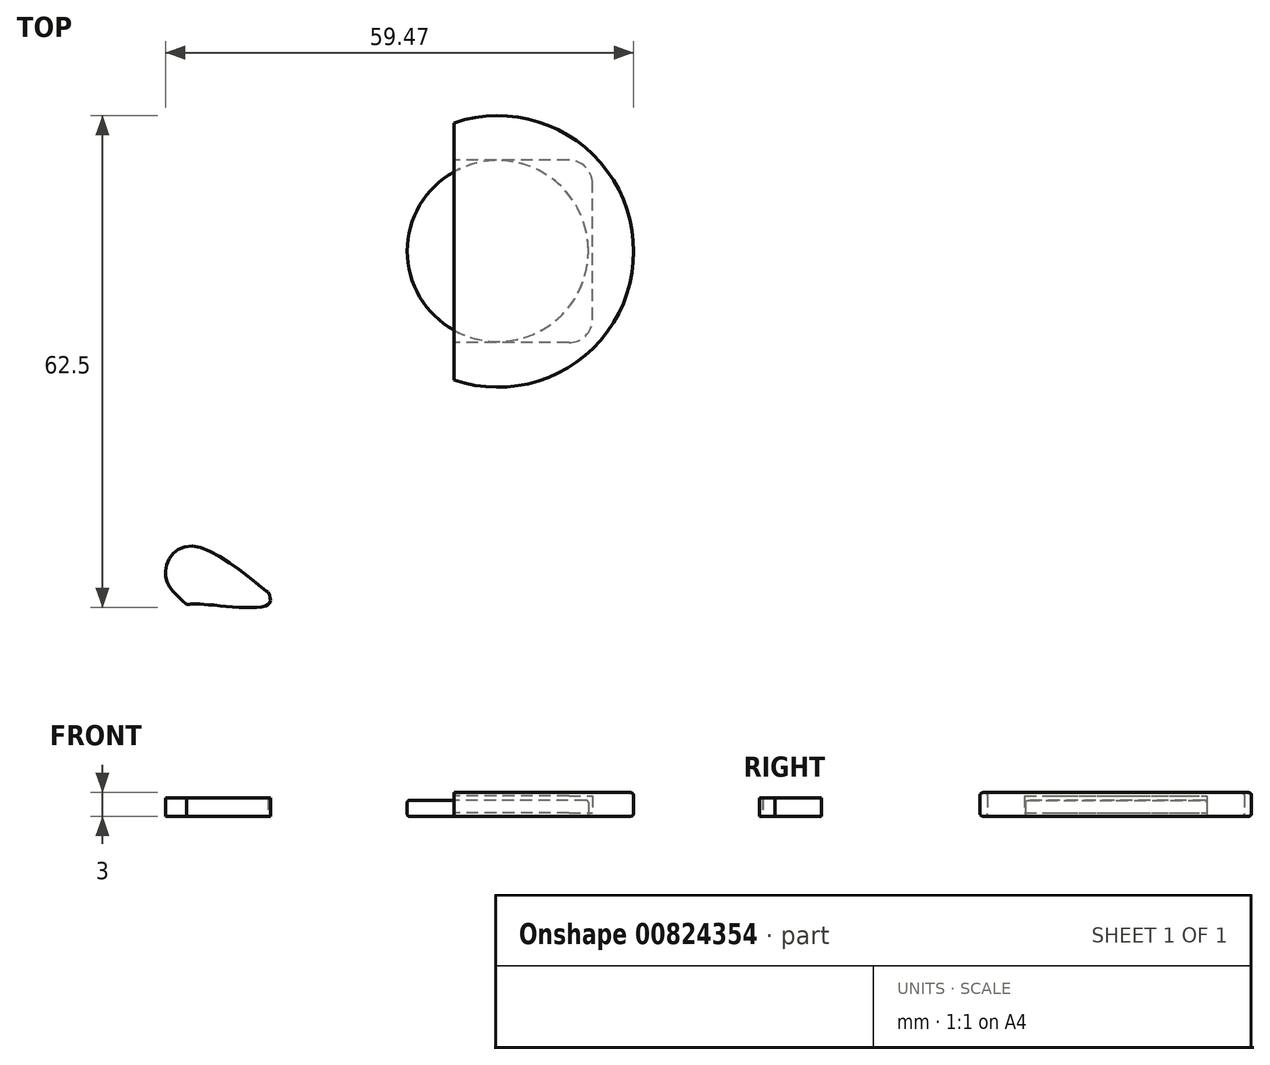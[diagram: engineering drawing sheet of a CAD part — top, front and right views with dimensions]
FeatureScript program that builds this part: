
annotation { "Feature Type Name" : "Feature", "Feature Type Description" : "" }
export const myFeature = defineFeature(function(context is Context, id is Id, definition is map)
    precondition{}
    {
        {
            var Q0;
            Q0=qCreatedBy(makeId("Top.planeOp"),FACE);
            var sketch = newSketch(context, id + "F0", { "sketchPlane" : qUnion([Q0])});
            skCircle(sketch, "E0", {"center": v(0, 0) * mm, "radius": 11.5 * mm});
            skSolve(sketch);
        }
        {
            var Q0;
            Q0=makeQuery(id+"F0.imprint","IMPRINT",FACE,{"disambiguationData":[TD([[makeQuery(id+"F0.imprint","IMPRINT",EDGE,{"derivedFrom":sQuery(id+"F0.wireOp",EDGE,"E0")}),1.0]])]});
            extrude(context, id + "F1", {"entities" : qUnion([Q0]), "depth" : 2 * mm, "offsetDistance" : 25 * mm});
        }
        {
            var Q0;
            Q0=makeQuery(id+"F1.opExtrude","CAP_EDGE",EDGE,{"disambiguationData":[OSD([sQuery(id+"F0.wireOp",EDGE,"E0")])],"isStart":false});
            var Q1;
            Q1=makeQuery(id+"F1.opExtrude","CAP_EDGE",EDGE,{"disambiguationData":[OSD([sQuery(id+"F0.wireOp",EDGE,"E0")])],"isStart":true});
            fillet(context, id + "F2", {"entities" : qUnion([Q0, Q1]), "radius" : 0.25 * mm, "tangentPropagation" : true, "allowEdgeOverflow" : false});
        }
        {
            var Q0;
            Q0=makeQuery(id+"F1.opExtrude","SWEPT_BODY",BODY,{"disambiguationData":[OSD([sQuery(id+"F0.wireOp",EDGE,"E0")])]});
            transform(context, id + "F3", {"entities" : qUnion([Q0]), "transformType" : TransformType.TRANSLATION_3D, "dx" : 0 * mm, "dy" : 36.3 * mm, "dz" : 0 * mm, "makeCopy" : true});
        }
        {
            var Q0;
            Q0=qCreatedBy(makeId("Top.planeOp"),FACE);
            var sketch = newSketch(context, id + "F4", { "sketchPlane" : qUnion([Q0])});
            skLineSegment(sketch, "E1.bottom", {"start": v(-15.7, 51.26) * mm, "end": v(-3.72, 51.26) * mm});
            skLineSegment(sketch, "E1.top", {"start": v(-15.7, 20.78) * mm, "end": v(-3.72, 20.78) * mm});
            skLineSegment(sketch, "E1.left", {"start": v(-15.7, 51.26) * mm, "end": v(-15.7, 20.78) * mm});
            skLineSegment(sketch, "E1.right", {"start": v(-3.72, 51.26) * mm, "end": v(-3.72, 20.78) * mm});
            skSolve(sketch);
        }
        {
            var Q0;
            Q0=makeQuery(id+"F4.imprint","IMPRINT",FACE,{"disambiguationData":[TD([[makeQuery(id+"F4.imprint","IMPRINT",EDGE,{"derivedFrom":sQuery(id+"F4.wireOp",EDGE,"E1.bottom")}),-1.0]])]});
            extrude(context, id + "F5", {"entities" : qUnion([Q0]), "depth" : 2 * mm, "offsetDistance" : 25 * mm});
        }
        {
            var Q0;
            Q0=makeQuery(id+"F5.opExtrude","SWEPT_BODY",BODY,{"disambiguationData":[OSD([sQuery(id+"F4.wireOp",EDGE,"E1.bottom"),sQuery(id+"F4.wireOp",EDGE,"E1.top"),sQuery(id+"F4.wireOp",EDGE,"E1.left"),sQuery(id+"F4.wireOp",EDGE,"E1.right")])]});
            var Q1;
            Q1=makeQuery(id+"F3.opPattern","COPY",BODY,{"derivedFrom":makeQuery(id+"F1.opExtrude","SWEPT_BODY",BODY,{"disambiguationData":[OSD([sQuery(id+"F0.wireOp",EDGE,"E0")])]}),"instanceName":"1"});
            booleanBodies(context, id + "F6", {"operationType" : BooleanOperationType.SUBTRACTION, "tools" : qUnion([Q0]), "targets" : qUnion([Q1])});
        }
        {
            var Q0;
            Q0=makeQuery(id+"F3.opPattern","COPY",BODY,{"derivedFrom":makeQuery(id+"F1.opExtrude","SWEPT_BODY",BODY,{"disambiguationData":[OSD([sQuery(id+"F0.wireOp",EDGE,"E0")])]}),"instanceName":"1"});
            var Q1;
            Q1=qCreatedBy(makeId("Origin.pointOp"),VERTEX);
            transform(context, id + "F7", {"entities" : qUnion([Q0]), "transformType" : TransformType.SCALE_UNIFORMLY, "scale" : 1.5, "scalePoint" : qUnion([Q1]), "makeCopy" : false});
        }
        {
            var Q0;
            Q0=makeQuery(id+"F6.opBoolean","COPY",FACE,{"derivedFrom":makeQuery(id+"F5.opExtrude","SWEPT_FACE",FACE,{"disambiguationData":[OSD([sQuery(id+"F4.wireOp",EDGE,"E1.right")])]})});
            var sketch = newSketch(context, id + "F8", { "sketchPlane" : qUnion([Q0])});
            skLineSegment(sketch, "E2", {"start": v(-38.52, 3) * mm, "end": v(-70.38, 3) * mm, "construction": true});
            skPoint(sketch, "E3", {"position": v(-54.45, 3) * mm});
            skLineSegment(sketch, "E4", {"start": v(-54.45, 3) * mm, "end": v(-54.45, 0) * mm, "construction": true});
            skPoint(sketch, "E5", {"position": v(-54.45, 1.5) * mm});
            skLineSegment(sketch, "E6.bottom", {"start": v(-42.85, 2.6) * mm, "end": v(-66.05, 2.6) * mm});
            skLineSegment(sketch, "E6.top", {"start": v(-42.85, 0.4) * mm, "end": v(-66.05, 0.4) * mm});
            skLineSegment(sketch, "E6.left", {"start": v(-42.85, 2.6) * mm, "end": v(-42.85, 0.4) * mm});
            skLineSegment(sketch, "E6.right", {"start": v(-66.05, 2.6) * mm, "end": v(-66.05, 0.4) * mm});
            skSolve(sketch);
        }
        {
            var Q0;
            Q0=makeQuery(id+"F8.imprint","IMPRINT",FACE,{"disambiguationData":[TD([[makeQuery(id+"F8.imprint","IMPRINT",EDGE,{"derivedFrom":sQuery(id+"F8.wireOp",EDGE,"E6.bottom")}),1.0]])]});
            extrude(context, id + "F9", {"entities" : qUnion([Q0]), "operationType" : NewBodyOperationType.REMOVE, "oppositeDirection" : true, "depth" : 17.6 * mm, "offsetDistance" : 25 * mm});
        }
        {
            var Q0;
            Q0=makeQuery(id+"F9.boolean.opBoolean","COPY",EDGE,{"derivedFrom":makeQuery(id+"F9.opExtrude","CAP_EDGE",EDGE,{"disambiguationData":[OSD([sQuery(id+"F8.wireOp",EDGE,"E6.right")])],"isStart":false})});
            var Q1;
            Q1=makeQuery(id+"F9.boolean.opBoolean","COPY",EDGE,{"derivedFrom":makeQuery(id+"F9.opExtrude","CAP_EDGE",EDGE,{"disambiguationData":[OSD([sQuery(id+"F8.wireOp",EDGE,"E6.left")])],"isStart":false})});
            fillet(context, id + "F10", {"entities" : qUnion([Q0, Q1]), "radius" : 3 * mm, "tangentPropagation" : true, "allowEdgeOverflow" : false});
        }
        {
            var Q0;
            Q0=makeQuery(id+"F1.opExtrude","SWEPT_BODY",BODY,{"disambiguationData":[OSD([sQuery(id+"F0.wireOp",EDGE,"E0")])]});
            transform(context, id + "F11", {"entities" : qUnion([Q0]), "transformType" : TransformType.TRANSLATION_3D, "dx" : 0 * mm, "dy" : 54.5 * mm, "dz" : 0 * mm, "makeCopy" : false});
        }
        {
            var Q0;
            Q0=makeQuery(id+"F1.opExtrude","SWEPT_BODY",BODY,{"disambiguationData":[OSD([sQuery(id+"F0.wireOp",EDGE,"E0")])]});
            var Q1;
            Q1=makeQuery(id+"F3.opPattern","COPY",BODY,{"derivedFrom":makeQuery(id+"F1.opExtrude","SWEPT_BODY",BODY,{"disambiguationData":[OSD([sQuery(id+"F0.wireOp",EDGE,"E0")])]}),"instanceName":"1"});
            transform(context, id + "F12", {"entities" : qUnion([Q0, Q1]), "transformType" : TransformType.TRANSLATION_3D, "dx" : 0 * mm, "dy" : -56.7 * mm, "dz" : 0 * mm, "makeCopy" : false});
        }
        {
            var Q0;
            Q0=qCreatedBy(makeId("Top.planeOp"),FACE);
            var sketch = newSketch(context, id + "F13", { "sketchPlane" : qUnion([Q0])});
            skFitSpline(sketch, "E7", {"points": [v(-39.5, -47.1) * mm, v(-42.22, -43.2) * mm, v(-38.6, -39.7) * mm, v(-29.15, -45.51) * mm, v(-29.3, -45.18) * mm, v(-29.23, -45.35) * mm], "startDerivative": vector(-16.07, 13.92) * mm, "endDerivative": vector(3, -5.64) * mm});
            skFitSpline(sketch, "E8", {"points": [v(-39.5, -47.1) * mm, v(-37.04, -47.1) * mm, v(-29.15, -47.1) * mm, v(-29.28, -45.26) * mm], "startDerivative": vector(6.46, 0.53) * mm, "endDerivative": vector(-4, 9.21) * mm});
            skSolve(sketch);
        }
        {
            var Q0;
            {var subQ0=sQuery(id+"F13.wireOp",EDGE,"E8");var subQ1=sQuery(id+"F13.wireOp",EDGE,"E7");var subQ2=makeQuery(id+"F13.imprint","INTERSECT",VERTEX,{"disambiguationData":[OD(0.0)],"derivedFrom":[subQ1,subQ0]});Q0=makeQuery(id+"F13.imprint","IMPRINT",FACE,{"disambiguationData":[TD([[makeQuery(id+"F13.imprint","IMPRINT",EDGE,{"disambiguationData":[TD([[subQ2,-1.0]])],"derivedFrom":subQ1}),-1.0]])]});}
            extrude(context, id + "F14", {"entities" : qUnion([Q0]), "depth" : 2.3 * mm, "offsetDistance" : 25 * mm});
        }
        {
            var Q0;
            Q0=makeQuery(id+"F14.opExtrude","SWEPT_BODY",BODY,{"disambiguationData":[OSD([sQuery(id+"F13.wireOp",EDGE,"E7"),sQuery(id+"F13.wireOp",EDGE,"E8")])]});
            transform(context, id + "F15", {"entities" : qUnion([Q0]), "transformType" : TransformType.COPY});
        }
    });
